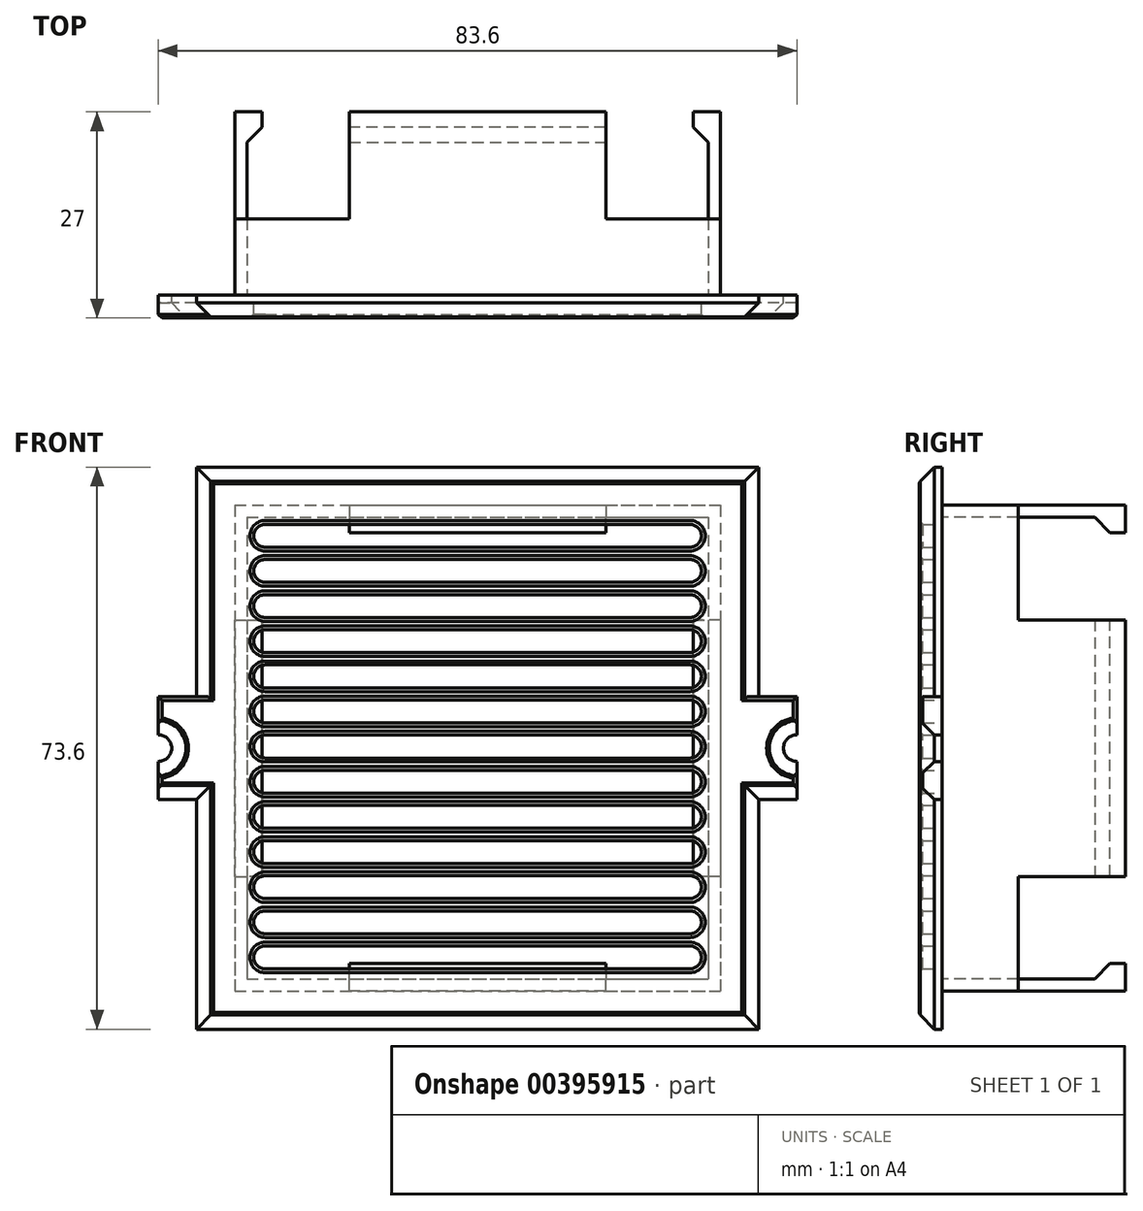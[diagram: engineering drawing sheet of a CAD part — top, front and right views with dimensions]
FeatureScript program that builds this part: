
annotation { "Feature Type Name" : "Feature", "Feature Type Description" : "" }
export const myFeature = defineFeature(function(context is Context, id is Id, definition is map)
    precondition{}
    {
        {
            var Q0;
            Q0=qCreatedBy(makeId("Front.planeOp"),FACE);
            var sketch = newSketch(context, id + "F0", { "sketchPlane" : qUnion([Q0])});
            skLineSegment(sketch, "E0.bottom", {"start": v(-30.2, 30.2) * mm, "end": v(30.2, 30.2) * mm});
            skLineSegment(sketch, "E0.top", {"start": v(-30.2, -30.2) * mm, "end": v(30.2, -30.2) * mm});
            skLineSegment(sketch, "E0.left", {"start": v(-30.2, 30.2) * mm, "end": v(-30.2, -30.2) * mm});
            skLineSegment(sketch, "E0.right", {"start": v(30.2, 30.2) * mm, "end": v(30.2, -30.2) * mm});
            skLineSegment(sketch, "E1.bottom", {"start": v(-36.8, 36.8) * mm, "end": v(36.8, 36.8) * mm});
            skLineSegment(sketch, "E1.top", {"start": v(-36.8, -36.8) * mm, "end": v(36.8, -36.8) * mm});
            skLineSegment(sketch, "E1.left", {"start": v(-36.8, 36.8) * mm, "end": v(-36.8, -36.8) * mm});
            skLineSegment(sketch, "E1.right", {"start": v(36.8, 36.8) * mm, "end": v(36.8, -36.8) * mm});
            skLineSegment(sketch, "E2.bottom", {"start": v(-31.8, 31.8) * mm, "end": v(31.8, 31.8) * mm});
            skLineSegment(sketch, "E2.top", {"start": v(-31.8, -31.8) * mm, "end": v(31.8, -31.8) * mm});
            skLineSegment(sketch, "E2.left", {"start": v(-31.8, 31.8) * mm, "end": v(-31.8, -31.8) * mm});
            skLineSegment(sketch, "E2.right", {"start": v(31.8, 31.8) * mm, "end": v(31.8, -31.8) * mm});
            skCircle(sketch, "E3", {"center": v(-41.8, 0) * mm, "radius": 1.75 * mm});
            skCircle(sketch, "E4", {"center": v(41.8, 0) * mm, "radius": 1.75 * mm});
            skLineSegment(sketch, "E5.bottom", {"start": v(-27.8, 29.3) * mm, "end": v(27.8, 29.3) * mm});
            skLineSegment(sketch, "E5.top", {"start": v(-27.8, 26.3) * mm, "end": v(27.8, 26.3) * mm});
            skLineSegment(sketch, "E5.left", {"start": v(-29.3, 27.8) * mm, "end": v(-29.3, 27.8) * mm});
            skLineSegment(sketch, "E5.right", {"start": v(29.3, 27.8) * mm, "end": v(29.3, 27.8) * mm});
            skPoint(sketch, "E6.visualSharp", {"position": v(-29.3, 29.3) * mm});
            skArc(sketch, "E6.filletArc", {"start": v(-27.8, 29.3) * mm, "mid": v(-28.86, 28.86) * mm, "end": v(-29.3, 27.8) * mm});
            skPoint(sketch, "E7.visualSharp", {"position": v(-29.3, 26.3) * mm});
            skArc(sketch, "E7.filletArc", {"start": v(-29.3, 27.8) * mm, "mid": v(-28.86, 26.74) * mm, "end": v(-27.8, 26.3) * mm});
            skPoint(sketch, "E8.visualSharp", {"position": v(29.3, 29.3) * mm});
            skArc(sketch, "E8.filletArc", {"start": v(29.3, 27.8) * mm, "mid": v(28.86, 28.86) * mm, "end": v(27.8, 29.3) * mm});
            skPoint(sketch, "E9.visualSharp", {"position": v(29.3, 26.3) * mm});
            skArc(sketch, "E9.filletArc", {"start": v(27.8, 26.3) * mm, "mid": v(28.86, 26.74) * mm, "end": v(29.3, 27.8) * mm});
            skLineSegment(sketch, "E10.0.1.0", {"start": v(-27.8, 21.7) * mm, "end": v(27.8, 21.7) * mm});
            skLineSegment(sketch, "E10.0.1.1", {"start": v(-27.8, 24.7) * mm, "end": v(27.8, 24.7) * mm});
            skPoint(sketch, "E10.0.1.2", {"position": v(-29.3, 24.7) * mm});
            skPoint(sketch, "E10.0.1.3", {"position": v(-29.3, 21.7) * mm});
            skPoint(sketch, "E10.0.1.4", {"position": v(29.3, 24.7) * mm});
            skPoint(sketch, "E10.0.1.5", {"position": v(29.3, 21.7) * mm});
            skArc(sketch, "E10.0.1.6", {"start": v(-29.3, 23.2) * mm, "mid": v(-28.86, 22.14) * mm, "end": v(-27.8, 21.7) * mm});
            skArc(sketch, "E10.0.1.7", {"start": v(27.8, 21.7) * mm, "mid": v(28.86, 22.14) * mm, "end": v(29.3, 23.2) * mm});
            skArc(sketch, "E10.0.1.8", {"start": v(29.3, 23.2) * mm, "mid": v(28.86, 24.26) * mm, "end": v(27.8, 24.7) * mm});
            skArc(sketch, "E10.0.1.9", {"start": v(-27.8, 24.7) * mm, "mid": v(-28.86, 24.26) * mm, "end": v(-29.3, 23.2) * mm});
            skLineSegment(sketch, "E10.0.2.0", {"start": v(-27.8, 17.1) * mm, "end": v(27.8, 17.1) * mm});
            skLineSegment(sketch, "E10.0.2.1", {"start": v(-27.8, 20.1) * mm, "end": v(27.8, 20.1) * mm});
            skPoint(sketch, "E10.0.2.2", {"position": v(-29.3, 20.1) * mm});
            skPoint(sketch, "E10.0.2.3", {"position": v(-29.3, 17.1) * mm});
            skPoint(sketch, "E10.0.2.4", {"position": v(29.3, 20.1) * mm});
            skPoint(sketch, "E10.0.2.5", {"position": v(29.3, 17.1) * mm});
            skArc(sketch, "E10.0.2.6", {"start": v(-29.3, 18.6) * mm, "mid": v(-28.86, 17.54) * mm, "end": v(-27.8, 17.1) * mm});
            skArc(sketch, "E10.0.2.7", {"start": v(27.8, 17.1) * mm, "mid": v(28.86, 17.54) * mm, "end": v(29.3, 18.6) * mm});
            skArc(sketch, "E10.0.2.8", {"start": v(29.3, 18.6) * mm, "mid": v(28.86, 19.66) * mm, "end": v(27.8, 20.1) * mm});
            skArc(sketch, "E10.0.2.9", {"start": v(-27.8, 20.1) * mm, "mid": v(-28.86, 19.66) * mm, "end": v(-29.3, 18.6) * mm});
            skLineSegment(sketch, "E10.0.3.0", {"start": v(-27.8, 12.5) * mm, "end": v(27.8, 12.5) * mm});
            skLineSegment(sketch, "E10.0.3.1", {"start": v(-27.8, 15.5) * mm, "end": v(27.8, 15.5) * mm});
            skPoint(sketch, "E10.0.3.2", {"position": v(-29.3, 15.5) * mm});
            skPoint(sketch, "E10.0.3.3", {"position": v(-29.3, 12.5) * mm});
            skPoint(sketch, "E10.0.3.4", {"position": v(29.3, 15.5) * mm});
            skPoint(sketch, "E10.0.3.5", {"position": v(29.3, 12.5) * mm});
            skArc(sketch, "E10.0.3.6", {"start": v(-29.3, 14) * mm, "mid": v(-28.86, 12.94) * mm, "end": v(-27.8, 12.5) * mm});
            skArc(sketch, "E10.0.3.7", {"start": v(27.8, 12.5) * mm, "mid": v(28.86, 12.94) * mm, "end": v(29.3, 14) * mm});
            skArc(sketch, "E10.0.3.8", {"start": v(29.3, 14) * mm, "mid": v(28.86, 15.06) * mm, "end": v(27.8, 15.5) * mm});
            skArc(sketch, "E10.0.3.9", {"start": v(-27.8, 15.5) * mm, "mid": v(-28.86, 15.06) * mm, "end": v(-29.3, 14) * mm});
            skLineSegment(sketch, "E10.0.4.0", {"start": v(-27.8, 7.9) * mm, "end": v(27.8, 7.9) * mm});
            skLineSegment(sketch, "E10.0.4.1", {"start": v(-27.8, 10.9) * mm, "end": v(27.8, 10.9) * mm});
            skPoint(sketch, "E10.0.4.2", {"position": v(-29.3, 10.9) * mm});
            skPoint(sketch, "E10.0.4.3", {"position": v(-29.3, 7.9) * mm});
            skPoint(sketch, "E10.0.4.4", {"position": v(29.3, 10.9) * mm});
            skPoint(sketch, "E10.0.4.5", {"position": v(29.3, 7.9) * mm});
            skArc(sketch, "E10.0.4.6", {"start": v(-29.3, 9.4) * mm, "mid": v(-28.86, 8.34) * mm, "end": v(-27.8, 7.9) * mm});
            skArc(sketch, "E10.0.4.7", {"start": v(27.8, 7.9) * mm, "mid": v(28.86, 8.34) * mm, "end": v(29.3, 9.4) * mm});
            skArc(sketch, "E10.0.4.8", {"start": v(29.3, 9.4) * mm, "mid": v(28.86, 10.46) * mm, "end": v(27.8, 10.9) * mm});
            skArc(sketch, "E10.0.4.9", {"start": v(-27.8, 10.9) * mm, "mid": v(-28.86, 10.46) * mm, "end": v(-29.3, 9.4) * mm});
            skLineSegment(sketch, "E10.0.5.0", {"start": v(-27.8, 3.3) * mm, "end": v(27.8, 3.3) * mm});
            skLineSegment(sketch, "E10.0.5.1", {"start": v(-27.8, 6.3) * mm, "end": v(27.8, 6.3) * mm});
            skPoint(sketch, "E10.0.5.2", {"position": v(-29.3, 6.3) * mm});
            skPoint(sketch, "E10.0.5.3", {"position": v(-29.3, 3.3) * mm});
            skPoint(sketch, "E10.0.5.4", {"position": v(29.3, 6.3) * mm});
            skPoint(sketch, "E10.0.5.5", {"position": v(29.3, 3.3) * mm});
            skArc(sketch, "E10.0.5.6", {"start": v(-29.3, 4.8) * mm, "mid": v(-28.86, 3.74) * mm, "end": v(-27.8, 3.3) * mm});
            skArc(sketch, "E10.0.5.7", {"start": v(27.8, 3.3) * mm, "mid": v(28.86, 3.74) * mm, "end": v(29.3, 4.8) * mm});
            skArc(sketch, "E10.0.5.8", {"start": v(29.3, 4.8) * mm, "mid": v(28.86, 5.86) * mm, "end": v(27.8, 6.3) * mm});
            skArc(sketch, "E10.0.5.9", {"start": v(-27.8, 6.3) * mm, "mid": v(-28.86, 5.86) * mm, "end": v(-29.3, 4.8) * mm});
            skLineSegment(sketch, "E10.0.6.0", {"start": v(-27.8, -1.3) * mm, "end": v(27.8, -1.3) * mm});
            skLineSegment(sketch, "E10.0.6.1", {"start": v(-27.8, 1.7) * mm, "end": v(27.8, 1.7) * mm});
            skPoint(sketch, "E10.0.6.2", {"position": v(-29.3, 1.7) * mm});
            skPoint(sketch, "E10.0.6.3", {"position": v(-29.3, -1.3) * mm});
            skPoint(sketch, "E10.0.6.4", {"position": v(29.3, 1.7) * mm});
            skPoint(sketch, "E10.0.6.5", {"position": v(29.3, -1.3) * mm});
            skArc(sketch, "E10.0.6.6", {"start": v(-29.3, 0.2) * mm, "mid": v(-28.86, -0.86) * mm, "end": v(-27.8, -1.3) * mm});
            skArc(sketch, "E10.0.6.7", {"start": v(27.8, -1.3) * mm, "mid": v(28.86, -0.86) * mm, "end": v(29.3, 0.2) * mm});
            skArc(sketch, "E10.0.6.8", {"start": v(29.3, 0.2) * mm, "mid": v(28.86, 1.26) * mm, "end": v(27.8, 1.7) * mm});
            skArc(sketch, "E10.0.6.9", {"start": v(-27.8, 1.7) * mm, "mid": v(-28.86, 1.26) * mm, "end": v(-29.3, 0.2) * mm});
            skLineSegment(sketch, "E10.0.7.0", {"start": v(-27.8, -5.9) * mm, "end": v(27.8, -5.9) * mm});
            skLineSegment(sketch, "E10.0.7.1", {"start": v(-27.8, -2.9) * mm, "end": v(27.8, -2.9) * mm});
            skPoint(sketch, "E10.0.7.2", {"position": v(-29.3, -2.9) * mm});
            skPoint(sketch, "E10.0.7.3", {"position": v(-29.3, -5.9) * mm});
            skPoint(sketch, "E10.0.7.4", {"position": v(29.3, -2.9) * mm});
            skPoint(sketch, "E10.0.7.5", {"position": v(29.3, -5.9) * mm});
            skArc(sketch, "E10.0.7.6", {"start": v(-29.3, -4.4) * mm, "mid": v(-28.86, -5.46) * mm, "end": v(-27.8, -5.9) * mm});
            skArc(sketch, "E10.0.7.7", {"start": v(27.8, -5.9) * mm, "mid": v(28.86, -5.46) * mm, "end": v(29.3, -4.4) * mm});
            skArc(sketch, "E10.0.7.8", {"start": v(29.3, -4.4) * mm, "mid": v(28.86, -3.34) * mm, "end": v(27.8, -2.9) * mm});
            skArc(sketch, "E10.0.7.9", {"start": v(-27.8, -2.9) * mm, "mid": v(-28.86, -3.34) * mm, "end": v(-29.3, -4.4) * mm});
            skLineSegment(sketch, "E10.0.8.0", {"start": v(-27.8, -10.5) * mm, "end": v(27.8, -10.5) * mm});
            skLineSegment(sketch, "E10.0.8.1", {"start": v(-27.8, -7.5) * mm, "end": v(27.8, -7.5) * mm});
            skPoint(sketch, "E10.0.8.2", {"position": v(-29.3, -7.5) * mm});
            skPoint(sketch, "E10.0.8.3", {"position": v(-29.3, -10.5) * mm});
            skPoint(sketch, "E10.0.8.4", {"position": v(29.3, -7.5) * mm});
            skPoint(sketch, "E10.0.8.5", {"position": v(29.3, -10.5) * mm});
            skArc(sketch, "E10.0.8.6", {"start": v(-29.3, -9) * mm, "mid": v(-28.86, -10.06) * mm, "end": v(-27.8, -10.5) * mm});
            skArc(sketch, "E10.0.8.7", {"start": v(27.8, -10.5) * mm, "mid": v(28.86, -10.06) * mm, "end": v(29.3, -9) * mm});
            skArc(sketch, "E10.0.8.8", {"start": v(29.3, -9) * mm, "mid": v(28.86, -7.94) * mm, "end": v(27.8, -7.5) * mm});
            skArc(sketch, "E10.0.8.9", {"start": v(-27.8, -7.5) * mm, "mid": v(-28.86, -7.94) * mm, "end": v(-29.3, -9) * mm});
            skLineSegment(sketch, "E10.0.9.0", {"start": v(-27.8, -15.1) * mm, "end": v(27.8, -15.1) * mm});
            skLineSegment(sketch, "E10.0.9.1", {"start": v(-27.8, -12.1) * mm, "end": v(27.8, -12.1) * mm});
            skPoint(sketch, "E10.0.9.2", {"position": v(-29.3, -12.1) * mm});
            skPoint(sketch, "E10.0.9.3", {"position": v(-29.3, -15.1) * mm});
            skPoint(sketch, "E10.0.9.4", {"position": v(29.3, -12.1) * mm});
            skPoint(sketch, "E10.0.9.5", {"position": v(29.3, -15.1) * mm});
            skArc(sketch, "E10.0.9.6", {"start": v(-29.3, -13.6) * mm, "mid": v(-28.86, -14.66) * mm, "end": v(-27.8, -15.1) * mm});
            skArc(sketch, "E10.0.9.7", {"start": v(27.8, -15.1) * mm, "mid": v(28.86, -14.66) * mm, "end": v(29.3, -13.6) * mm});
            skArc(sketch, "E10.0.9.8", {"start": v(29.3, -13.6) * mm, "mid": v(28.86, -12.54) * mm, "end": v(27.8, -12.1) * mm});
            skArc(sketch, "E10.0.9.9", {"start": v(-27.8, -12.1) * mm, "mid": v(-28.86, -12.54) * mm, "end": v(-29.3, -13.6) * mm});
            skLineSegment(sketch, "E10.0.10.0", {"start": v(-27.8, -19.7) * mm, "end": v(27.8, -19.7) * mm});
            skLineSegment(sketch, "E10.0.10.1", {"start": v(-27.8, -16.7) * mm, "end": v(27.8, -16.7) * mm});
            skPoint(sketch, "E10.0.10.2", {"position": v(-29.3, -16.7) * mm});
            skPoint(sketch, "E10.0.10.3", {"position": v(-29.3, -19.7) * mm});
            skPoint(sketch, "E10.0.10.4", {"position": v(29.3, -16.7) * mm});
            skPoint(sketch, "E10.0.10.5", {"position": v(29.3, -19.7) * mm});
            skArc(sketch, "E10.0.10.6", {"start": v(-29.3, -18.2) * mm, "mid": v(-28.86, -19.26) * mm, "end": v(-27.8, -19.7) * mm});
            skArc(sketch, "E10.0.10.7", {"start": v(27.8, -19.7) * mm, "mid": v(28.86, -19.26) * mm, "end": v(29.3, -18.2) * mm});
            skArc(sketch, "E10.0.10.8", {"start": v(29.3, -18.2) * mm, "mid": v(28.86, -17.14) * mm, "end": v(27.8, -16.7) * mm});
            skArc(sketch, "E10.0.10.9", {"start": v(-27.8, -16.7) * mm, "mid": v(-28.86, -17.14) * mm, "end": v(-29.3, -18.2) * mm});
            skLineSegment(sketch, "E10.0.11.0", {"start": v(-27.8, -24.3) * mm, "end": v(27.8, -24.3) * mm});
            skLineSegment(sketch, "E10.0.11.1", {"start": v(-27.8, -21.3) * mm, "end": v(27.8, -21.3) * mm});
            skPoint(sketch, "E10.0.11.2", {"position": v(-29.3, -21.3) * mm});
            skPoint(sketch, "E10.0.11.3", {"position": v(-29.3, -24.3) * mm});
            skPoint(sketch, "E10.0.11.4", {"position": v(29.3, -21.3) * mm});
            skPoint(sketch, "E10.0.11.5", {"position": v(29.3, -24.3) * mm});
            skArc(sketch, "E10.0.11.6", {"start": v(-29.3, -22.8) * mm, "mid": v(-28.86, -23.86) * mm, "end": v(-27.8, -24.3) * mm});
            skArc(sketch, "E10.0.11.7", {"start": v(27.8, -24.3) * mm, "mid": v(28.86, -23.86) * mm, "end": v(29.3, -22.8) * mm});
            skArc(sketch, "E10.0.11.8", {"start": v(29.3, -22.8) * mm, "mid": v(28.86, -21.74) * mm, "end": v(27.8, -21.3) * mm});
            skArc(sketch, "E10.0.11.9", {"start": v(-27.8, -21.3) * mm, "mid": v(-28.86, -21.74) * mm, "end": v(-29.3, -22.8) * mm});
            skLineSegment(sketch, "E10.0.12.0", {"start": v(-27.8, -28.9) * mm, "end": v(27.8, -28.9) * mm});
            skLineSegment(sketch, "E10.0.12.1", {"start": v(-27.8, -25.9) * mm, "end": v(27.8, -25.9) * mm});
            skPoint(sketch, "E10.0.12.2", {"position": v(-29.3, -25.9) * mm});
            skPoint(sketch, "E10.0.12.3", {"position": v(-29.3, -28.9) * mm});
            skPoint(sketch, "E10.0.12.4", {"position": v(29.3, -25.9) * mm});
            skPoint(sketch, "E10.0.12.5", {"position": v(29.3, -28.9) * mm});
            skArc(sketch, "E10.0.12.6", {"start": v(-29.3, -27.4) * mm, "mid": v(-28.86, -28.46) * mm, "end": v(-27.8, -28.9) * mm});
            skArc(sketch, "E10.0.12.7", {"start": v(27.8, -28.9) * mm, "mid": v(28.86, -28.46) * mm, "end": v(29.3, -27.4) * mm});
            skArc(sketch, "E10.0.12.8", {"start": v(29.3, -27.4) * mm, "mid": v(28.86, -26.34) * mm, "end": v(27.8, -25.9) * mm});
            skArc(sketch, "E10.0.12.9", {"start": v(-27.8, -25.9) * mm, "mid": v(-28.86, -26.34) * mm, "end": v(-29.3, -27.4) * mm});
            skLineSegment(sketch, "E10.direction1", {"start": v(-29.3, 26.3) * mm, "end": v(-3.3, 26.3) * mm, "construction": true});
            skLineSegment(sketch, "E10.direction2", {"start": v(-29.3, 26.3) * mm, "end": v(-29.3, 21.7) * mm, "construction": true});
            skCircle(sketch, "E11.0", {"center": v(-41.8, 0) * mm, "radius": 6.75 * mm});
            skCircle(sketch, "E12.0", {"center": v(41.8, 0) * mm, "radius": 6.75 * mm});
            skLineSegment(sketch, "E13", {"start": v(-36.8, 6.75) * mm, "end": v(-41.8, 6.75) * mm});
            skLineSegment(sketch, "E14", {"start": v(-41.8, 6.75) * mm, "end": v(-41.8, -6.75) * mm});
            skLineSegment(sketch, "E15", {"start": v(-41.8, -6.75) * mm, "end": v(-36.8, -6.75) * mm});
            skLineSegment(sketch, "E16", {"start": v(36.8, 6.75) * mm, "end": v(41.8, 6.75) * mm});
            skLineSegment(sketch, "E17", {"start": v(41.8, 6.75) * mm, "end": v(41.8, -6.75) * mm});
            skLineSegment(sketch, "E18", {"start": v(41.8, -6.75) * mm, "end": v(36.8, -6.75) * mm});
            skSolve(sketch);
        }
        {
            var Q0;
            {var subQ6=sQuery(id+"F0.wireOp",EDGE,"E1.bottom");Q0=makeQuery(id+"F0.imprint","IMPRINT",FACE,{"disambiguationData":[TD([[makeQuery(id+"F0.imprint","IMPRINT",EDGE,{"derivedFrom":subQ6}),-1.0]])]});}
            var Q1;
            {var subQ1=sQuery(id+"F0.wireOp",EDGE,"E11.0");var subQ3=sQuery(id+"F0.wireOp",EDGE,"E1.left");var subQ6=makeQuery(id+"F0.imprint","INTERSECT",VERTEX,{"disambiguationData":[OD(0.0)],"derivedFrom":[subQ3,subQ1]});Q1=makeQuery(id+"F0.imprint","IMPRINT",FACE,{"disambiguationData":[TD([[makeQuery(id+"F0.imprint","IMPRINT",EDGE,{"disambiguationData":[TD([[subQ6,-1.0]])],"derivedFrom":subQ3}),-1.0]])]});}
            var Q2;
            {var subQ0=sQuery(id+"F0.wireOp",EDGE,"E13");Q2=makeQuery(id+"F0.imprint","IMPRINT",FACE,{"disambiguationData":[TD([[makeQuery(id+"F0.imprint","IMPRINT",EDGE,{"derivedFrom":subQ0}),1.0]])]});}
            var Q3;
            {var subQ0=sQuery(id+"F0.wireOp",EDGE,"E14");var subQ1=sQuery(id+"F0.wireOp",EDGE,"E3");var subQ2=makeQuery(id+"F0.imprint","INTERSECT",VERTEX,{"disambiguationData":[OD(0.0)],"derivedFrom":[subQ1,subQ0]});Q3=makeQuery(id+"F0.imprint","IMPRINT",FACE,{"disambiguationData":[TD([[makeQuery(id+"F0.imprint","IMPRINT",EDGE,{"disambiguationData":[TD([[subQ2,-1.0]])],"derivedFrom":subQ1}),-1.0]])]});}
            var Q4;
            {var subQ0=sQuery(id+"F0.wireOp",EDGE,"E11.0");var subQ1=sQuery(id+"F0.wireOp",EDGE,"E1.left");var subQ2=makeQuery(id+"F0.imprint","INTERSECT",VERTEX,{"disambiguationData":[OD(0.0)],"derivedFrom":[subQ1,subQ0]});Q4=makeQuery(id+"F0.imprint","IMPRINT",FACE,{"disambiguationData":[TD([[makeQuery(id+"F0.imprint","IMPRINT",EDGE,{"disambiguationData":[TD([[subQ2,-1.0]])],"derivedFrom":subQ1}),1.0]])]});}
            var Q5;
            {var subQ0=sQuery(id+"F0.wireOp",EDGE,"E15");Q5=makeQuery(id+"F0.imprint","IMPRINT",FACE,{"disambiguationData":[TD([[makeQuery(id+"F0.imprint","IMPRINT",EDGE,{"derivedFrom":subQ0}),1.0]])]});}
            var Q6;
            {var subQ0=sQuery(id+"F0.wireOp",EDGE,"E18");Q6=makeQuery(id+"F0.imprint","IMPRINT",FACE,{"disambiguationData":[TD([[makeQuery(id+"F0.imprint","IMPRINT",EDGE,{"derivedFrom":subQ0}),-1.0]])]});}
            var Q7;
            {var subQ1=sQuery(id+"F0.wireOp",EDGE,"E12.0");var subQ3=sQuery(id+"F0.wireOp",EDGE,"E1.right");var subQ4=makeQuery(id+"F0.imprint","INTERSECT",VERTEX,{"disambiguationData":[OD(0.0)],"derivedFrom":[subQ3,subQ1]});Q7=makeQuery(id+"F0.imprint","IMPRINT",FACE,{"disambiguationData":[TD([[makeQuery(id+"F0.imprint","IMPRINT",EDGE,{"disambiguationData":[TD([[subQ4,-1.0]])],"derivedFrom":subQ3}),1.0]])]});}
            var Q8;
            {var subQ0=sQuery(id+"F0.wireOp",EDGE,"E12.0");var subQ1=sQuery(id+"F0.wireOp",EDGE,"E1.right");var subQ2=makeQuery(id+"F0.imprint","INTERSECT",VERTEX,{"disambiguationData":[OD(0.0)],"derivedFrom":[subQ1,subQ0]});Q8=makeQuery(id+"F0.imprint","IMPRINT",FACE,{"disambiguationData":[TD([[makeQuery(id+"F0.imprint","IMPRINT",EDGE,{"disambiguationData":[TD([[subQ2,-1.0]])],"derivedFrom":subQ1}),-1.0]])]});}
            var Q9;
            {var subQ0=sQuery(id+"F0.wireOp",EDGE,"E16");Q9=makeQuery(id+"F0.imprint","IMPRINT",FACE,{"disambiguationData":[TD([[makeQuery(id+"F0.imprint","IMPRINT",EDGE,{"derivedFrom":subQ0}),-1.0]])]});}
            var Q10;
            {var subQ0=sQuery(id+"F0.wireOp",EDGE,"E17");var subQ1=sQuery(id+"F0.wireOp",EDGE,"E4");var subQ2=makeQuery(id+"F0.imprint","INTERSECT",VERTEX,{"disambiguationData":[OD(0.0)],"derivedFrom":[subQ1,subQ0]});Q10=makeQuery(id+"F0.imprint","IMPRINT",FACE,{"disambiguationData":[TD([[makeQuery(id+"F0.imprint","IMPRINT",EDGE,{"disambiguationData":[TD([[subQ2,1.0]])],"derivedFrom":subQ1}),-1.0]])]});}
            var Q11;
            Q11=makeQuery(id+"F0.imprint","IMPRINT",FACE,{"disambiguationData":[TD([[makeQuery(id+"F0.imprint","IMPRINT",EDGE,{"derivedFrom":sQuery(id+"F0.wireOp",EDGE,"E0.bottom")}),1.0]])]});
            var Q12;
            Q12=makeQuery(id+"F0.imprint","IMPRINT",FACE,{"disambiguationData":[TD([[makeQuery(id+"F0.imprint","IMPRINT",EDGE,{"derivedFrom":sQuery(id+"F0.wireOp",EDGE,"E0.bottom")}),-1.0]])]});
            extrude(context, id + "F1", {"entities" : qUnion([Q0, Q1, Q2, Q3, Q4, Q5, Q6, Q7, Q8, Q9, Q10, Q11, Q12]), "depth" : 3 * mm});
        }
        {
            var Q0;
            {var subQ0=sQuery(id+"F0.wireOp",EDGE,"E1.left");Q0=makeQuery(id+"F1.opExtrude","CAP_EDGE",EDGE,{"disambiguationData":[OSD([subQ0]),TDD([makeQuery(id+"F0.imprint","IMPRINT",EDGE,{"disambiguationData":[TD([[makeQuery(id+"F0.imprint","INTERSECT",VERTEX,{"derivedFrom":[sQuery(id+"F0.wireOp",EDGE,"E1.top"),subQ0]}),1.0]])],"derivedFrom":subQ0})])],"isStart":false});}
            var Q1;
            Q1=makeQuery(id+"F1.opExtrude","CAP_EDGE",EDGE,{"disambiguationData":[OSD([sQuery(id+"F0.wireOp",EDGE,"E15")])],"isStart":false});
            var Q2;
            {var subQ0=sQuery(id+"F0.wireOp",EDGE,"E1.left");Q2=makeQuery(id+"F1.opExtrude","CAP_EDGE",EDGE,{"disambiguationData":[OSD([subQ0]),TDD([makeQuery(id+"F0.imprint","IMPRINT",EDGE,{"disambiguationData":[TD([[makeQuery(id+"F0.imprint","INTERSECT",VERTEX,{"derivedFrom":[sQuery(id+"F0.wireOp",EDGE,"E1.bottom"),subQ0]}),-1.0]])],"derivedFrom":subQ0})])],"isStart":false});}
            var Q3;
            Q3=makeQuery(id+"F1.opExtrude","CAP_EDGE",EDGE,{"disambiguationData":[OSD([sQuery(id+"F0.wireOp",EDGE,"E1.bottom")])],"isStart":false});
            var Q4;
            Q4=makeQuery(id+"F1.opExtrude","CAP_EDGE",EDGE,{"disambiguationData":[OSD([sQuery(id+"F0.wireOp",EDGE,"E1.top")])],"isStart":false});
            var Q5;
            Q5=makeQuery(id+"F1.opExtrude","CAP_EDGE",EDGE,{"disambiguationData":[OSD([sQuery(id+"F0.wireOp",EDGE,"E18")])],"isStart":false});
            var Q6;
            {var subQ0=sQuery(id+"F0.wireOp",EDGE,"E1.right");Q6=makeQuery(id+"F1.opExtrude","CAP_EDGE",EDGE,{"disambiguationData":[OSD([subQ0]),TDD([makeQuery(id+"F0.imprint","IMPRINT",EDGE,{"disambiguationData":[TD([[makeQuery(id+"F0.imprint","INTERSECT",VERTEX,{"derivedFrom":[sQuery(id+"F0.wireOp",EDGE,"E1.top"),subQ0]}),1.0]])],"derivedFrom":subQ0})])],"isStart":false});}
            var Q7;
            {var subQ0=sQuery(id+"F0.wireOp",EDGE,"E1.right");Q7=makeQuery(id+"F1.opExtrude","CAP_EDGE",EDGE,{"disambiguationData":[OSD([subQ0]),TDD([makeQuery(id+"F0.imprint","IMPRINT",EDGE,{"disambiguationData":[TD([[makeQuery(id+"F0.imprint","INTERSECT",VERTEX,{"derivedFrom":[sQuery(id+"F0.wireOp",EDGE,"E1.bottom"),subQ0]}),-1.0]])],"derivedFrom":subQ0})])],"isStart":false});}
            chamfer(context, id + "F2", {"entities" : qUnion([Q0, Q1, Q2, Q3, Q4, Q5, Q6, Q7]), "width" : 2 * mm, "tangentPropagation" : true});
        }
        {
            var Q0;
            Q0=makeQuery(id+"F0.imprint","IMPRINT",FACE,{"disambiguationData":[TD([[makeQuery(id+"F0.imprint","IMPRINT",EDGE,{"derivedFrom":sQuery(id+"F0.wireOp",EDGE,"E0.bottom")}),1.0]])]});
            extrude(context, id + "F3", {"entities" : qUnion([Q0]), "operationType" : NewBodyOperationType.ADD, "oppositeDirection" : true, "depth" : 10 * mm});
        }
        {
            var Q0;
            Q0=makeQuery(id+"F3.opExtrude","CAP_FACE",FACE,{"disambiguationData":[OSD([sQuery(id+"F0.wireOp",EDGE,"E0.bottom"),sQuery(id+"F0.wireOp",EDGE,"E0.top"),sQuery(id+"F0.wireOp",EDGE,"E0.left"),sQuery(id+"F0.wireOp",EDGE,"E0.right"),sQuery(id+"F0.wireOp",EDGE,"E2.bottom"),sQuery(id+"F0.wireOp",EDGE,"E2.top"),sQuery(id+"F0.wireOp",EDGE,"E2.left"),sQuery(id+"F0.wireOp",EDGE,"E2.right")])],"isStart":false});
            var sketch = newSketch(context, id + "F4", { "sketchPlane" : qUnion([Q0])});
            skLineSegment(sketch, "E19.bottom", {"start": v(-31.8, 31.8) * mm, "end": v(-16.8, 31.8) * mm});
            skLineSegment(sketch, "E19.top", {"start": v(-31.8, 16.8) * mm, "end": v(-16.8, 16.8) * mm});
            skLineSegment(sketch, "E19.left", {"start": v(-31.8, 31.8) * mm, "end": v(-31.8, 16.8) * mm});
            skLineSegment(sketch, "E19.right", {"start": v(-16.8, 31.8) * mm, "end": v(-16.8, 16.8) * mm});
            skLineSegment(sketch, "E20.MirrorCS", {"start": v(16.8, 31.8) * mm, "end": v(16.8, 16.8) * mm});
            skLineSegment(sketch, "E21.MirrorCS", {"start": v(31.8, 16.8) * mm, "end": v(16.8, 16.8) * mm});
            skLineSegment(sketch, "E22.MirrorCS", {"start": v(31.8, 31.8) * mm, "end": v(31.8, 16.8) * mm});
            skLineSegment(sketch, "E23.MirrorCS", {"start": v(31.8, 31.8) * mm, "end": v(16.8, 31.8) * mm});
            skLineSegment(sketch, "E24.MirrorCS", {"start": v(-31.8, -16.8) * mm, "end": v(-16.8, -16.8) * mm});
            skLineSegment(sketch, "E25.MirrorCS", {"start": v(-16.8, -31.8) * mm, "end": v(-16.8, -16.8) * mm});
            skLineSegment(sketch, "E26.MirrorCS", {"start": v(-31.8, -31.8) * mm, "end": v(-16.8, -31.8) * mm});
            skLineSegment(sketch, "E27.MirrorCS", {"start": v(-31.8, -31.8) * mm, "end": v(-31.8, -16.8) * mm});
            skLineSegment(sketch, "E28.MirrorCS", {"start": v(16.8, -31.8) * mm, "end": v(16.8, -16.8) * mm});
            skLineSegment(sketch, "E29.MirrorCS", {"start": v(31.8, -31.8) * mm, "end": v(16.8, -31.8) * mm});
            skLineSegment(sketch, "E30.MirrorCS", {"start": v(31.8, -16.8) * mm, "end": v(16.8, -16.8) * mm});
            skLineSegment(sketch, "E31.MirrorCS", {"start": v(31.8, -31.8) * mm, "end": v(31.8, -16.8) * mm});
            skSolve(sketch);
        }
        {
            var Q0;
            {var subQ0=sQuery(id+"F4.wireOp",EDGE,"E19.top");var subQ3=makeQuery(id+"F3.opExtrude","CAP_EDGE",EDGE,{"disambiguationData":[OSD([sQuery(id+"F0.wireOp",EDGE,"E0.right")])],"isStart":false});var subQ4=makeQuery(id+"F4.imprint","INTERSECT",VERTEX,{"derivedFrom":[subQ3,subQ0]});Q0=makeQuery(id+"F4.imprint","IMPRINT",FACE,{"disambiguationData":[TD([[makeQuery(id+"F4.imprint","IMPRINT",EDGE,{"disambiguationData":[TD([[subQ4,-1.0]])],"derivedFrom":subQ3}),-1.0]])]});}
            var Q1;
            {var subQ0=sQuery(id+"F4.wireOp",EDGE,"E19.right");var subQ3=makeQuery(id+"F3.opExtrude","CAP_EDGE",EDGE,{"disambiguationData":[OSD([sQuery(id+"F0.wireOp",EDGE,"E0.bottom")])],"isStart":false});var subQ4=makeQuery(id+"F4.imprint","INTERSECT",VERTEX,{"derivedFrom":[subQ3,subQ0]});Q1=makeQuery(id+"F4.imprint","IMPRINT",FACE,{"disambiguationData":[TD([[makeQuery(id+"F4.imprint","IMPRINT",EDGE,{"disambiguationData":[TD([[subQ4,1.0]])],"derivedFrom":subQ3}),-1.0]])]});}
            var Q2;
            {var subQ0=sQuery(id+"F4.wireOp",EDGE,"E21.MirrorCS");var subQ3=makeQuery(id+"F3.opExtrude","CAP_EDGE",EDGE,{"disambiguationData":[OSD([sQuery(id+"F0.wireOp",EDGE,"E0.left")])],"isStart":false});var subQ4=makeQuery(id+"F4.imprint","INTERSECT",VERTEX,{"derivedFrom":[subQ3,subQ0]});Q2=makeQuery(id+"F4.imprint","IMPRINT",FACE,{"disambiguationData":[TD([[makeQuery(id+"F4.imprint","IMPRINT",EDGE,{"disambiguationData":[TD([[subQ4,-1.0]])],"derivedFrom":subQ3}),1.0]])]});}
            var Q3;
            {var subQ0=sQuery(id+"F4.wireOp",EDGE,"E25.MirrorCS");var subQ3=makeQuery(id+"F3.opExtrude","CAP_EDGE",EDGE,{"disambiguationData":[OSD([sQuery(id+"F0.wireOp",EDGE,"E0.top")])],"isStart":false});var subQ4=makeQuery(id+"F4.imprint","INTERSECT",VERTEX,{"derivedFrom":[subQ3,subQ0]});Q3=makeQuery(id+"F4.imprint","IMPRINT",FACE,{"disambiguationData":[TD([[makeQuery(id+"F4.imprint","IMPRINT",EDGE,{"disambiguationData":[TD([[subQ4,1.0]])],"derivedFrom":subQ3}),1.0]])]});}
            extrude(context, id + "F5", {"entities" : qUnion([Q0, Q1, Q2, Q3]), "operationType" : NewBodyOperationType.ADD, "depth" : 10 * mm});
        }
        {
            var Q0;
            Q0=makeQuery(id+"F5.opExtrude","CAP_FACE",FACE,{"disambiguationData":[OSD([sQuery(id+"F0.wireOp",EDGE,"E0.bottom"),sQuery(id+"F0.wireOp",EDGE,"E2.bottom"),sQuery(id+"F4.wireOp",EDGE,"E19.right"),sQuery(id+"F4.wireOp",EDGE,"E20.MirrorCS")])],"isStart":false});
            var sketch = newSketch(context, id + "F6", { "sketchPlane" : qUnion([Q0])});
            skLineSegment(sketch, "E32.bottom", {"start": v(-16.8, 31.8) * mm, "end": v(16.8, 31.8) * mm});
            skLineSegment(sketch, "E32.top", {"start": v(-16.8, 28.2) * mm, "end": v(16.8, 28.2) * mm});
            skLineSegment(sketch, "E32.left", {"start": v(-16.8, 31.8) * mm, "end": v(-16.8, 28.2) * mm});
            skLineSegment(sketch, "E32.right", {"start": v(16.8, 31.8) * mm, "end": v(16.8, 28.2) * mm});
            skLineSegment(sketch, "E33.bottom", {"start": v(-31.8, 16.8) * mm, "end": v(-28.2, 16.8) * mm});
            skLineSegment(sketch, "E33.top", {"start": v(-31.8, -16.8) * mm, "end": v(-28.2, -16.8) * mm});
            skLineSegment(sketch, "E33.left", {"start": v(-31.8, 16.8) * mm, "end": v(-31.8, -16.8) * mm});
            skLineSegment(sketch, "E33.right", {"start": v(-28.2, 16.8) * mm, "end": v(-28.2, -16.8) * mm});
            skLineSegment(sketch, "E34.bottom", {"start": v(-16.8, -31.8) * mm, "end": v(16.8, -31.8) * mm});
            skLineSegment(sketch, "E34.top", {"start": v(-16.8, -28.2) * mm, "end": v(16.8, -28.2) * mm});
            skLineSegment(sketch, "E34.left", {"start": v(-16.8, -31.8) * mm, "end": v(-16.8, -28.2) * mm});
            skLineSegment(sketch, "E34.right", {"start": v(16.8, -31.8) * mm, "end": v(16.8, -28.2) * mm});
            skLineSegment(sketch, "E35.bottom", {"start": v(31.8, -16.8) * mm, "end": v(28.2, -16.8) * mm});
            skLineSegment(sketch, "E35.top", {"start": v(31.8, 16.8) * mm, "end": v(28.2, 16.8) * mm});
            skLineSegment(sketch, "E35.left", {"start": v(31.8, -16.8) * mm, "end": v(31.8, 16.8) * mm});
            skLineSegment(sketch, "E35.right", {"start": v(28.2, -16.8) * mm, "end": v(28.2, 16.8) * mm});
            skSolve(sketch);
        }
        {
            var Q0;
            Q0 = qSketchRegion(id + "F6", true);
            extrude(context, id + "F7", {"entities" : qUnion([Q0]), "operationType" : NewBodyOperationType.ADD, "depth" : 4 * mm});
        }
        {
            var Q0;
            Q0=makeQuery(id+"F7.opExtrude","CAP_EDGE",EDGE,{"disambiguationData":[OSD([sQuery(id+"F6.wireOp",EDGE,"E35.right")])],"isStart":true});
            var Q1;
            Q1=makeQuery(id+"F7.opExtrude","CAP_EDGE",EDGE,{"disambiguationData":[OSD([sQuery(id+"F6.wireOp",EDGE,"E34.top")])],"isStart":true});
            var Q2;
            Q2=makeQuery(id+"F7.opExtrude","CAP_EDGE",EDGE,{"disambiguationData":[OSD([sQuery(id+"F6.wireOp",EDGE,"E33.right")])],"isStart":true});
            var Q3;
            Q3=makeQuery(id+"F7.opExtrude","CAP_EDGE",EDGE,{"disambiguationData":[OSD([sQuery(id+"F6.wireOp",EDGE,"E32.top")])],"isStart":true});
            chamfer(context, id + "F8", {"entities" : qUnion([Q0, Q1, Q2, Q3]), "width" : 2 * mm, "tangentPropagation" : true});
        }
        {
            var Q0;
            Q0=makeQuery(id+"F1.opExtrude","CAP_EDGE",EDGE,{"disambiguationData":[OSD([sQuery(id+"F0.wireOp",EDGE,"E4")])],"isStart":false});
            var Q1;
            Q1=makeQuery(id+"F1.opExtrude","CAP_EDGE",EDGE,{"disambiguationData":[OSD([sQuery(id+"F0.wireOp",EDGE,"E3")])],"isStart":false});
            chamfer(context, id + "F9", {"entities" : qUnion([Q0, Q1]), "width" : 2 * mm, "tangentPropagation" : true});
        }
        {
            var Q0;
            Q0=makeQuery(id+"F1.opExtrude","CAP_FACE",FACE,{"disambiguationData":[OSD([sQuery(id+"F0.wireOp",EDGE,"E1.bottom"),sQuery(id+"F0.wireOp",EDGE,"E1.top"),sQuery(id+"F0.wireOp",EDGE,"E1.left"),sQuery(id+"F0.wireOp",EDGE,"E1.right"),sQuery(id+"F0.wireOp",EDGE,"E3"),sQuery(id+"F0.wireOp",EDGE,"E4"),sQuery(id+"F0.wireOp",EDGE,"E5.bottom"),sQuery(id+"F0.wireOp",EDGE,"E5.top"),sQuery(id+"F0.wireOp",EDGE,"E6.filletArc"),sQuery(id+"F0.wireOp",EDGE,"E7.filletArc"),sQuery(id+"F0.wireOp",EDGE,"E8.filletArc"),sQuery(id+"F0.wireOp",EDGE,"E9.filletArc"),sQuery(id+"F0.wireOp",EDGE,"E10.0.1.0"),sQuery(id+"F0.wireOp",EDGE,"E10.0.1.1"),sQuery(id+"F0.wireOp",EDGE,"E10.0.1.6"),sQuery(id+"F0.wireOp",EDGE,"E10.0.1.7"),sQuery(id+"F0.wireOp",EDGE,"E10.0.1.8"),sQuery(id+"F0.wireOp",EDGE,"E10.0.1.9"),sQuery(id+"F0.wireOp",EDGE,"E10.0.2.0"),sQuery(id+"F0.wireOp",EDGE,"E10.0.2.1"),sQuery(id+"F0.wireOp",EDGE,"E10.0.2.6"),sQuery(id+"F0.wireOp",EDGE,"E10.0.2.7"),sQuery(id+"F0.wireOp",EDGE,"E10.0.2.8"),sQuery(id+"F0.wireOp",EDGE,"E10.0.2.9"),sQuery(id+"F0.wireOp",EDGE,"E10.0.3.0"),sQuery(id+"F0.wireOp",EDGE,"E10.0.3.1"),sQuery(id+"F0.wireOp",EDGE,"E10.0.3.6"),sQuery(id+"F0.wireOp",EDGE,"E10.0.3.7"),sQuery(id+"F0.wireOp",EDGE,"E10.0.3.8"),sQuery(id+"F0.wireOp",EDGE,"E10.0.3.9"),sQuery(id+"F0.wireOp",EDGE,"E10.0.4.0"),sQuery(id+"F0.wireOp",EDGE,"E10.0.4.1"),sQuery(id+"F0.wireOp",EDGE,"E10.0.4.6"),sQuery(id+"F0.wireOp",EDGE,"E10.0.4.7"),sQuery(id+"F0.wireOp",EDGE,"E10.0.4.8"),sQuery(id+"F0.wireOp",EDGE,"E10.0.4.9"),sQuery(id+"F0.wireOp",EDGE,"E10.0.5.0"),sQuery(id+"F0.wireOp",EDGE,"E10.0.5.1"),sQuery(id+"F0.wireOp",EDGE,"E10.0.5.6"),sQuery(id+"F0.wireOp",EDGE,"E10.0.5.7"),sQuery(id+"F0.wireOp",EDGE,"E10.0.5.8"),sQuery(id+"F0.wireOp",EDGE,"E10.0.5.9"),sQuery(id+"F0.wireOp",EDGE,"E10.0.6.0"),sQuery(id+"F0.wireOp",EDGE,"E10.0.6.1"),sQuery(id+"F0.wireOp",EDGE,"E10.0.6.6"),sQuery(id+"F0.wireOp",EDGE,"E10.0.6.7"),sQuery(id+"F0.wireOp",EDGE,"E10.0.6.8"),sQuery(id+"F0.wireOp",EDGE,"E10.0.6.9"),sQuery(id+"F0.wireOp",EDGE,"E10.0.7.0"),sQuery(id+"F0.wireOp",EDGE,"E10.0.7.1"),sQuery(id+"F0.wireOp",EDGE,"E10.0.7.6"),sQuery(id+"F0.wireOp",EDGE,"E10.0.7.7"),sQuery(id+"F0.wireOp",EDGE,"E10.0.7.8"),sQuery(id+"F0.wireOp",EDGE,"E10.0.7.9"),sQuery(id+"F0.wireOp",EDGE,"E10.0.8.0"),sQuery(id+"F0.wireOp",EDGE,"E10.0.8.1"),sQuery(id+"F0.wireOp",EDGE,"E10.0.8.6"),sQuery(id+"F0.wireOp",EDGE,"E10.0.8.7"),sQuery(id+"F0.wireOp",EDGE,"E10.0.8.8"),sQuery(id+"F0.wireOp",EDGE,"E10.0.8.9"),sQuery(id+"F0.wireOp",EDGE,"E10.0.9.0"),sQuery(id+"F0.wireOp",EDGE,"E10.0.9.1"),sQuery(id+"F0.wireOp",EDGE,"E10.0.9.6"),sQuery(id+"F0.wireOp",EDGE,"E10.0.9.7"),sQuery(id+"F0.wireOp",EDGE,"E10.0.9.8"),sQuery(id+"F0.wireOp",EDGE,"E10.0.9.9"),sQuery(id+"F0.wireOp",EDGE,"E10.0.10.0"),sQuery(id+"F0.wireOp",EDGE,"E10.0.10.1"),sQuery(id+"F0.wireOp",EDGE,"E10.0.10.6"),sQuery(id+"F0.wireOp",EDGE,"E10.0.10.7"),sQuery(id+"F0.wireOp",EDGE,"E10.0.10.8"),sQuery(id+"F0.wireOp",EDGE,"E10.0.10.9"),sQuery(id+"F0.wireOp",EDGE,"E10.0.11.0"),sQuery(id+"F0.wireOp",EDGE,"E10.0.11.1"),sQuery(id+"F0.wireOp",EDGE,"E10.0.11.6"),sQuery(id+"F0.wireOp",EDGE,"E10.0.11.7"),sQuery(id+"F0.wireOp",EDGE,"E10.0.11.8"),sQuery(id+"F0.wireOp",EDGE,"E10.0.11.9"),sQuery(id+"F0.wireOp",EDGE,"E10.0.12.0"),sQuery(id+"F0.wireOp",EDGE,"E10.0.12.1"),sQuery(id+"F0.wireOp",EDGE,"E10.0.12.6"),sQuery(id+"F0.wireOp",EDGE,"E10.0.12.7"),sQuery(id+"F0.wireOp",EDGE,"E10.0.12.8"),sQuery(id+"F0.wireOp",EDGE,"E10.0.12.9"),sQuery(id+"F0.wireOp",EDGE,"E11.0"),sQuery(id+"F0.wireOp",EDGE,"E12.0"),sQuery(id+"F0.wireOp",EDGE,"E13"),sQuery(id+"F0.wireOp",EDGE,"E15"),sQuery(id+"F0.wireOp",EDGE,"E16"),sQuery(id+"F0.wireOp",EDGE,"E18")])],"isStart":false});
            chamfer(context, id + "F10", {"entities" : qUnion([Q0]), "width" : .5 * mm, "tangentPropagation" : true});
        }
    });
